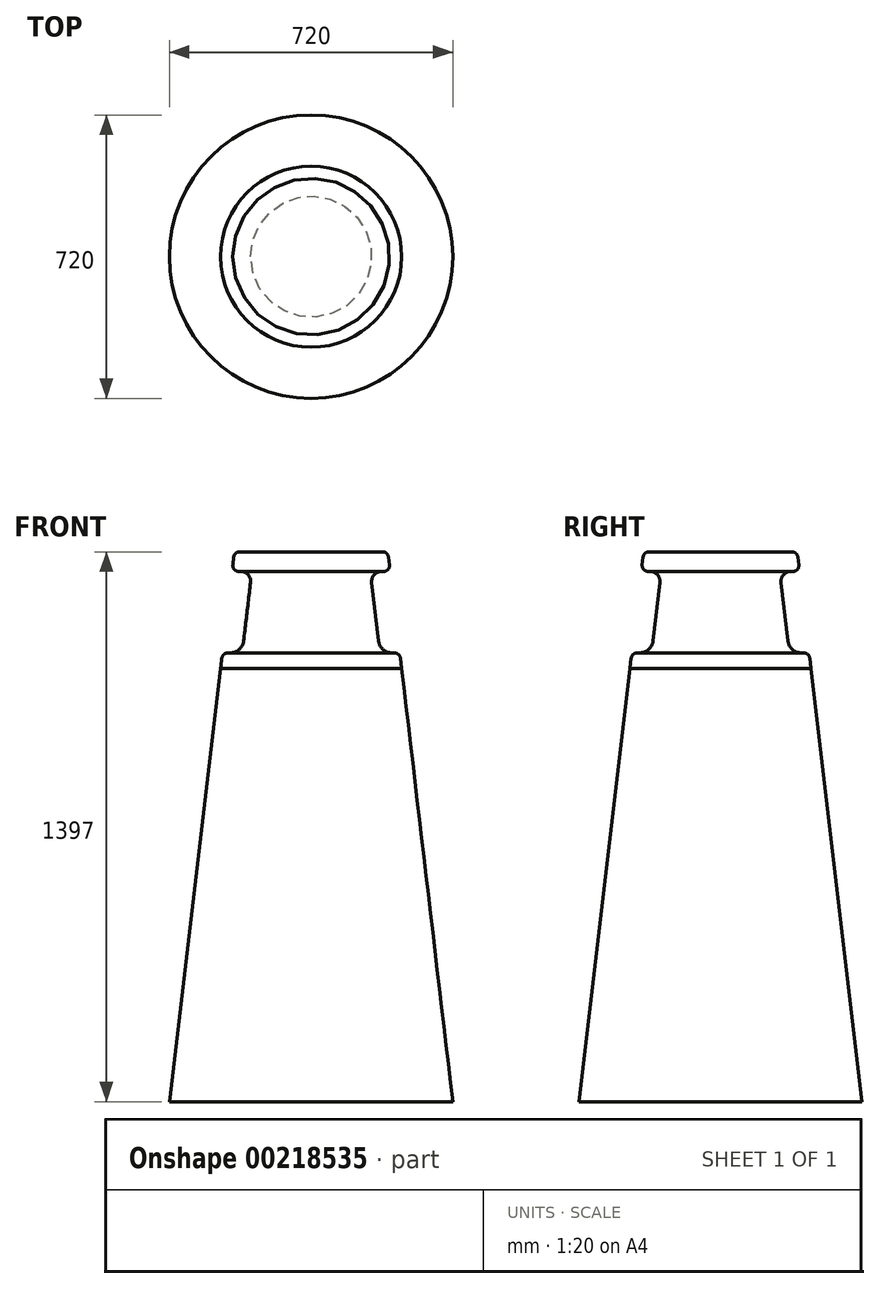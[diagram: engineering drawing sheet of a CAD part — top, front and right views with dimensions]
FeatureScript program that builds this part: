
annotation { "Feature Type Name" : "Feature", "Feature Type Description" : "" }
export const myFeature = defineFeature(function(context is Context, id is Id, definition is map)
    precondition{}
    {
        {
            var Q0;
            Q0=qCreatedBy(makeId("Front.planeOp"),FACE);
            var sketch = newSketch(context, id + "F0", { "sketchPlane" : qUnion([Q0])});
            skLineSegment(sketch, "E0", {"start": v(-360, 0) * mm, "end": v(0, 0) * mm});
            skLineSegment(sketch, "E1", {"start": v(-360, 0) * mm, "end": v(-230.08, 1100) * mm});
            skLineSegment(sketch, "E2", {"start": v(-230.08, 1100) * mm, "end": v(0, 1100) * mm});
            skLineSegment(sketch, "E3", {"start": v(0, 0) * mm, "end": v(0, 1434.25) * mm, "construction": true});
            skLineSegment(sketch, "E4", {"start": v(-230.08, 1100) * mm, "end": v(-226.92, 1126.76) * mm});
            skLineSegment(sketch, "E5", {"start": v(-181.67, 1397) * mm, "end": v(0, 1397) * mm});
            skLineSegment(sketch, "E6", {"start": v(-184.03, 1347) * mm, "end": v(-178.68, 1347) * mm});
            skLineSegment(sketch, "E7.0", {"start": v(-171.36, 1170.9) * mm, "end": v(-153.86, 1319.07) * mm});
            skLineSegment(sketch, "E8", {"start": v(-212.02, 1140) * mm, "end": v(-206.12, 1140) * mm});
            skLineSegment(sketch, "E9.trimOffspring", {"start": v(-198.93, 1363.76) * mm, "end": v(-196.56, 1383.76) * mm});
            skArc(sketch, "E10.filletArc", {"start": v(-212.02, 1140) * mm, "mid": v(-221.99, 1136.21) * mm, "end": v(-226.92, 1126.76) * mm});
            skArc(sketch, "E11.filletArc", {"start": v(-198.93, 1363.76) * mm, "mid": v(-195.24, 1352.03) * mm, "end": v(-184.03, 1347) * mm});
            skPoint(sketch, "E12.newPointA", {"position": v(-158.18, 1140) * mm});
            skArc(sketch, "E12.filletArc", {"start": v(-206.12, 1140) * mm, "mid": v(-182.86, 1148.84) * mm, "end": v(-171.36, 1170.9) * mm});
            skArc(sketch, "E13.filletArc", {"start": v(-153.86, 1319.07) * mm, "mid": v(-160, 1338.6) * mm, "end": v(-178.68, 1347) * mm});
            skPoint(sketch, "E14.visualSharp", {"position": v(-195, 1397) * mm});
            skArc(sketch, "E14.filletArc", {"start": v(-181.67, 1397) * mm, "mid": v(-191.63, 1393.21) * mm, "end": v(-196.56, 1383.76) * mm});
            skLineSegment(sketch, "E15", {"start": v(0, 1100) * mm, "end": v(0, 0) * mm});
            skLineSegment(sketch, "E16", {"start": v(0, 1100) * mm, "end": v(0, 1397) * mm});
            skSolve(sketch);
        }
        {
            var Q0;
            Q0=makeQuery(id+"F0.imprint","IMPRINT",FACE,{"disambiguationData":[TD([[makeQuery(id+"F0.imprint","IMPRINT",EDGE,{"derivedFrom":sQuery(id+"F0.wireOp",EDGE,"E2")}),1.0]])]});
            var Q1;
            Q1=sQuery(id+"F0.wireOp",EDGE,"E5");
            var Q2;
            Q2=sQuery(id+"F0.wireOp",EDGE,"E14.filletArc");
            var Q3;
            Q3=sQuery(id+"F0.wireOp",EDGE,"E9.trimOffspring");
            var Q4;
            Q4=sQuery(id+"F0.wireOp",EDGE,"E11.filletArc");
            var Q5;
            Q5=sQuery(id+"F0.wireOp",EDGE,"E6");
            var Q6;
            Q6=sQuery(id+"F0.wireOp",EDGE,"E13.filletArc");
            var Q7;
            Q7=sQuery(id+"F0.wireOp",EDGE,"E7.0");
            var Q8;
            Q8=sQuery(id+"F0.wireOp",EDGE,"E12.filletArc");
            var Q9;
            Q9=sQuery(id+"F0.wireOp",EDGE,"E8");
            var Q10;
            Q10=sQuery(id+"F0.wireOp",EDGE,"E10.filletArc");
            var Q11;
            Q11=sQuery(id+"F0.wireOp",EDGE,"E4");
            var Q12;
            Q12=sQuery(id+"F0.wireOp",EDGE,"E3");
            revolve(context, id + "F1", {"entities" : qUnion([Q0]), "surfaceEntities" : qUnion([Q1, Q2, Q3, Q4, Q5, Q6, Q7, Q8, Q9, Q10, Q11]), "axis" : qUnion([Q12]), "revolveType" : RevolveType.FULL});
        }
        {
            var Q0;
            Q0=makeQuery(id+"F0.imprint","IMPRINT",FACE,{"disambiguationData":[TD([[makeQuery(id+"F0.imprint","IMPRINT",EDGE,{"derivedFrom":sQuery(id+"F0.wireOp",EDGE,"E0")}),1.0]])]});
            var Q1;
            Q1=sQuery(id+"F0.wireOp",EDGE,"E15");
            revolve(context, id + "F2", {"entities" : qUnion([Q0]), "axis" : qUnion([Q1]), "revolveType" : RevolveType.FULL});
        }
    });
